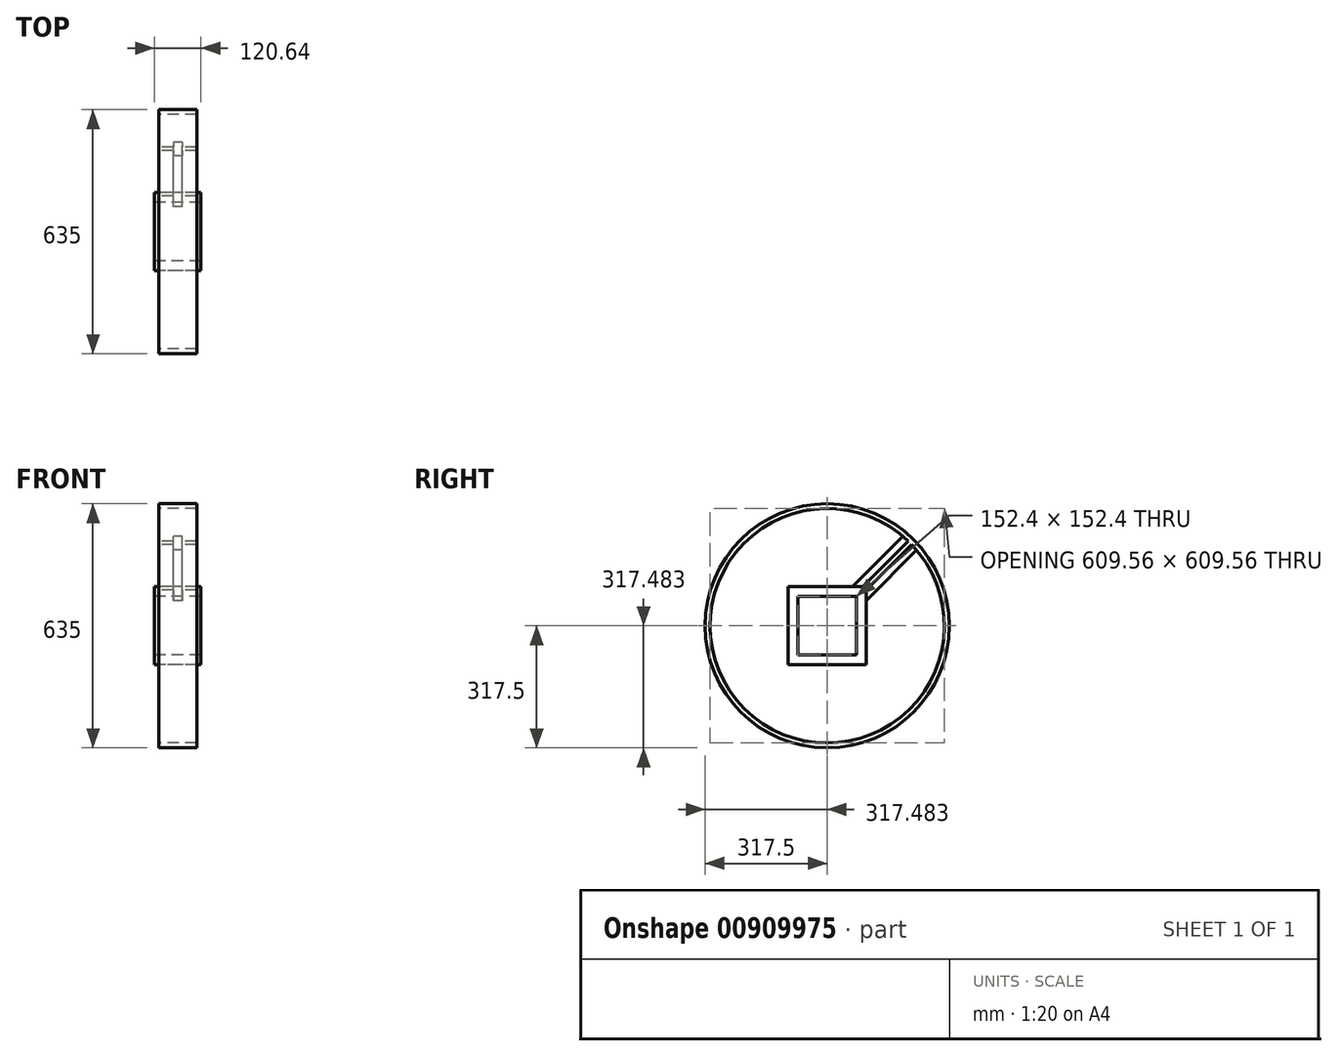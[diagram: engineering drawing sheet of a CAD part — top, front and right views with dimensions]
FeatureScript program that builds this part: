
annotation { "Feature Type Name" : "Feature", "Feature Type Description" : "" }
export const myFeature = defineFeature(function(context is Context, id is Id, definition is map)
    precondition{}
    {
        {
            var Q0;
            Q0=qCreatedBy(makeId("Right.planeOp"),FACE);
            var sketch = newSketch(context, id + "F0", { "sketchPlane" : qUnion([Q0])});
            skCircle(sketch, "E0", {"center": v(0, 0) * mm, "radius": 317.5 * mm});
            skCircle(sketch, "E1", {"center": v(0, 0) * mm, "radius": 304.8 * mm});
            skLineSegment(sketch, "E2.bottom", {"start": v(-76.2, 76.2) * mm, "end": v(76.2, 76.2) * mm});
            skLineSegment(sketch, "E2.top", {"start": v(-76.2, -76.2) * mm, "end": v(76.2, -76.2) * mm});
            skLineSegment(sketch, "E2.left", {"start": v(-76.2, 76.2) * mm, "end": v(-76.2, -76.2) * mm});
            skLineSegment(sketch, "E2.right", {"start": v(76.2, 76.2) * mm, "end": v(76.2, -76.2) * mm});
            skLineSegment(sketch, "E3.bottom", {"start": v(-101.6, 101.6) * mm, "end": v(101.6, 101.6) * mm});
            skLineSegment(sketch, "E3.top", {"start": v(-101.6, -101.6) * mm, "end": v(101.6, -101.6) * mm});
            skLineSegment(sketch, "E3.left", {"start": v(-101.6, 101.6) * mm, "end": v(-101.6, -101.6) * mm});
            skLineSegment(sketch, "E3.right", {"start": v(101.6, 101.6) * mm, "end": v(101.6, -101.6) * mm});
            skLineSegment(sketch, "E4", {"start": v(-101.6, 101.6) * mm, "end": v(101.6, -101.6) * mm, "construction": true});
            skLineSegment(sketch, "E5", {"start": v(101.6, 101.6) * mm, "end": v(-101.6, -101.6) * mm, "construction": true});
            skLineSegment(sketch, "E6", {"start": v(92.62, 101.6) * mm, "end": v(210.99, 219.97) * mm});
            skLineSegment(sketch, "E7", {"start": v(65.68, 101.6) * mm, "end": v(196.82, 232.74) * mm});
            skLineSegment(sketch, "E8", {"start": v(101.6, 92.62) * mm, "end": v(219.97, 210.99) * mm});
            skLineSegment(sketch, "E9", {"start": v(101.6, 65.68) * mm, "end": v(232.74, 196.82) * mm});
            skSolve(sketch);
        }
        {
            var Q0;
            Q0=makeQuery(id+"F0.imprint","IMPRINT",FACE,{"disambiguationData":[TD([[makeQuery(id+"F0.imprint","IMPRINT",EDGE,{"derivedFrom":sQuery(id+"F0.wireOp",EDGE,"E2.bottom")}),1.0]])]});
            extrude(context, id + "F1", {"entities" : qUnion([Q0]), "depth" : 120.65 * mm, "offsetDistance" : 25 * mm, "symmetric" : true});
        }
        {
            var Q0;
            {var subQ4=sQuery(id+"F0.wireOp",EDGE,"E6");Q0=makeQuery(id+"F0.imprint","IMPRINT",FACE,{"disambiguationData":[TD([[makeQuery(id+"F0.imprint","IMPRINT",EDGE,{"derivedFrom":subQ4}),-1.0]])]});}
            extrude(context, id + "F2", {"entities" : qUnion([Q0]), "operationType" : NewBodyOperationType.ADD, "depth" : 98.42 * mm, "offsetDistance" : 25 * mm, "symmetric" : true});
        }
        {
            var Q0;
            {var subQ0=sQuery(id+"F0.wireOp",EDGE,"E6");Q0=makeQuery(id+"F0.imprint","IMPRINT",FACE,{"disambiguationData":[TD([[makeQuery(id+"F0.imprint","IMPRINT",EDGE,{"derivedFrom":subQ0}),1.0]])]});}
            var Q1;
            {var subQ0=sQuery(id+"F0.wireOp",EDGE,"E8");Q1=makeQuery(id+"F0.imprint","IMPRINT",FACE,{"disambiguationData":[TD([[makeQuery(id+"F0.imprint","IMPRINT",EDGE,{"derivedFrom":subQ0}),-1.0]])]});}
            extrude(context, id + "F3", {"entities" : qUnion([Q0, Q1]), "operationType" : NewBodyOperationType.ADD, "depth" : 22.23 * mm, "offsetDistance" : 25 * mm, "symmetric" : true});
        }
        {
            var Q0;
            Q0=makeQuery(id+"F0.imprint","IMPRINT",FACE,{"disambiguationData":[TD([[makeQuery(id+"F0.imprint","IMPRINT",EDGE,{"derivedFrom":sQuery(id+"F0.wireOp",EDGE,"E0")}),1.0]])]});
            extrude(context, id + "F4", {"entities" : qUnion([Q0]), "operationType" : NewBodyOperationType.ADD, "depth" : 98.42 * mm, "offsetDistance" : 25 * mm, "symmetric" : true});
        }
    });
